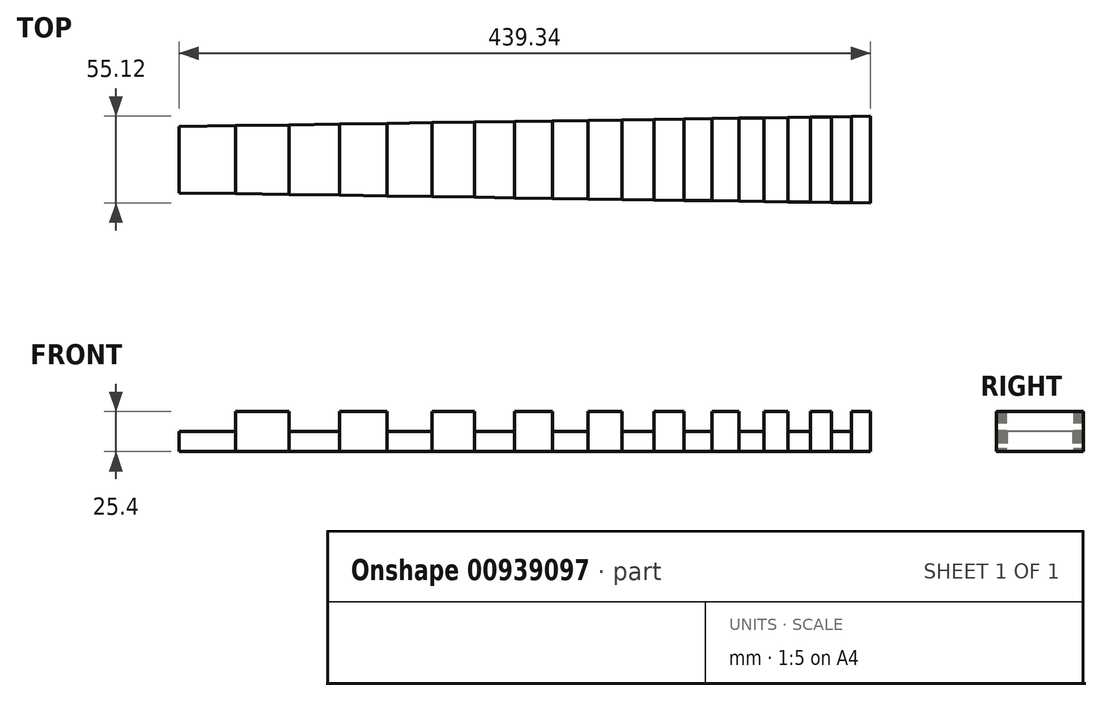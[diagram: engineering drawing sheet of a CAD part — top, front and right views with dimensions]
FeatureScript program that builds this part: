
annotation { "Feature Type Name" : "Feature", "Feature Type Description" : "" }
export const myFeature = defineFeature(function(context is Context, id is Id, definition is map)
    precondition{}
    {
        {
            var Q0;
            Q0=qCreatedBy(makeId("Top.planeOp"),FACE);
            var sketch = newSketch(context, id + "F0", { "sketchPlane" : qUnion([Q0])});
            skLineSegment(sketch, "E0", {"start": v(-189.34, 0) * mm, "end": v(250, 0) * mm});
            skLineSegment(sketch, "E1", {"start": v(-189.34, 21.08) * mm, "end": v(-189.34, -21.08) * mm});
            skPoint(sketch, "E2", {"position": v(-189.34, 0) * mm});
            skLineSegment(sketch, "E3", {"start": v(-153.35, 21.61) * mm, "end": v(-153.35, -21.61) * mm});
            skPoint(sketch, "E4", {"position": v(-153.35, 0) * mm});
            skLineSegment(sketch, "E5", {"start": v(-28.46, 23.45) * mm, "end": v(-28.46, -23.45) * mm});
            skPoint(sketch, "E6", {"position": v(-28.46, 0) * mm});
            skLineSegment(sketch, "E7", {"start": v(-87.31, 22.59) * mm, "end": v(-87.31, -22.59) * mm});
            skPoint(sketch, "E8", {"position": v(-87.31, 0) * mm});
            skLineSegment(sketch, "E9", {"start": v(-57.03, 23.03) * mm, "end": v(-57.03, -23.03) * mm});
            skPoint(sketch, "E10", {"position": v(-57.03, 0) * mm});
            skLineSegment(sketch, "E11", {"start": v(-119.36, 22.11) * mm, "end": v(-119.36, -22.11) * mm});
            skPoint(sketch, "E12", {"position": v(-119.36, 0) * mm});
            skLineSegment(sketch, "E13", {"start": v(112.26, 25.53) * mm, "end": v(112.26, -25.53) * mm});
            skPoint(sketch, "E14", {"position": v(112.26, 0) * mm});
            skLineSegment(sketch, "E15", {"start": v(131.33, 25.8) * mm, "end": v(131.33, -25.8) * mm});
            skPoint(sketch, "E16", {"position": v(131.33, 0) * mm});
            skLineSegment(sketch, "E17", {"start": v(149.34, 26.08) * mm, "end": v(149.34, -26.08) * mm});
            skPoint(sketch, "E18", {"position": v(149.34, 0) * mm});
            skLineSegment(sketch, "E19", {"start": v(166.33, 26.33) * mm, "end": v(166.33, -26.33) * mm});
            skPoint(sketch, "E20", {"position": v(166.33, 0) * mm});
            skLineSegment(sketch, "E21", {"start": v(197.5, 26.78) * mm, "end": v(197.5, -26.78) * mm});
            skPoint(sketch, "E22", {"position": v(197.5, 0) * mm});
            skLineSegment(sketch, "E23", {"start": v(70.65, 24.91) * mm, "end": v(70.65, -24.91) * mm});
            skPoint(sketch, "E24", {"position": v(70.65, 0) * mm});
            skLineSegment(sketch, "E25", {"start": v(92.06, 25.23) * mm, "end": v(92.06, -25.23) * mm});
            skPoint(sketch, "E26", {"position": v(92.06, 0) * mm});
            skLineSegment(sketch, "E27", {"start": v(211.77, 27) * mm, "end": v(211.77, -27) * mm});
            skPoint(sketch, "E28", {"position": v(211.77, 0) * mm});
            skLineSegment(sketch, "E29", {"start": v(250, 27.56) * mm, "end": v(250, -27.56) * mm});
            skPoint(sketch, "E30", {"position": v(250, 0) * mm});
            skLineSegment(sketch, "E31", {"start": v(-189.34, 21.08) * mm, "end": v(250, 27.56) * mm});
            skLineSegment(sketch, "E32", {"start": v(-189.34, -21.08) * mm, "end": v(250, -27.56) * mm});
            skLineSegment(sketch, "E33", {"start": v(-1.48, 23.85) * mm, "end": v(-1.48, -23.85) * mm});
            skPoint(sketch, "E34", {"position": v(-1.48, 0) * mm});
            skLineSegment(sketch, "E35", {"start": v(23.97, 24.23) * mm, "end": v(23.97, -24.23) * mm});
            skPoint(sketch, "E36", {"position": v(23.97, 0) * mm});
            skLineSegment(sketch, "E37", {"start": v(47.97, 24.58) * mm, "end": v(47.97, -24.58) * mm});
            skPoint(sketch, "E38", {"position": v(47.97, 0) * mm});
            skLineSegment(sketch, "E39", {"start": v(182.36, 26.56) * mm, "end": v(182.36, -26.56) * mm});
            skPoint(sketch, "E40", {"position": v(182.36, 0) * mm});
            skLineSegment(sketch, "E41", {"start": v(225.26, 27.2) * mm, "end": v(225.26, -27.2) * mm});
            skPoint(sketch, "E42", {"position": v(225.26, 0) * mm});
            skLineSegment(sketch, "E43", {"start": v(237.99, 27.38) * mm, "end": v(237.99, -27.38) * mm});
            skPoint(sketch, "E44", {"position": v(237.99, 0) * mm});
            skSolve(sketch);
        }
        {
            var Q0;
            {var subQ0=sQuery(id+"F0.wireOp",EDGE,"E3");var subQ1=sQuery(id+"F0.wireOp",EDGE,"E0");var subQ2=makeQuery(id+"F0.imprint","INTERSECT",VERTEX,{"derivedFrom":[subQ1,subQ0]});Q0=makeQuery(id+"F0.imprint","IMPRINT",FACE,{"disambiguationData":[TD([[makeQuery(id+"F0.imprint","IMPRINT",EDGE,{"disambiguationData":[TD([[subQ2,-1.0]])],"derivedFrom":subQ1}),1.0]])]});}
            var Q1;
            {var subQ0=sQuery(id+"F0.wireOp",EDGE,"E3");var subQ1=sQuery(id+"F0.wireOp",EDGE,"E0");var subQ2=makeQuery(id+"F0.imprint","INTERSECT",VERTEX,{"derivedFrom":[subQ1,subQ0]});Q1=makeQuery(id+"F0.imprint","IMPRINT",FACE,{"disambiguationData":[TD([[makeQuery(id+"F0.imprint","IMPRINT",EDGE,{"disambiguationData":[TD([[subQ2,-1.0]])],"derivedFrom":subQ1}),-1.0]])]});}
            var Q2;
            {var subQ0=sQuery(id+"F0.wireOp",EDGE,"E7");var subQ1=sQuery(id+"F0.wireOp",EDGE,"E0");var subQ2=makeQuery(id+"F0.imprint","INTERSECT",VERTEX,{"derivedFrom":[subQ1,subQ0]});Q2=makeQuery(id+"F0.imprint","IMPRINT",FACE,{"disambiguationData":[TD([[makeQuery(id+"F0.imprint","IMPRINT",EDGE,{"disambiguationData":[TD([[subQ2,-1.0]])],"derivedFrom":subQ1}),1.0]])]});}
            var Q3;
            {var subQ0=sQuery(id+"F0.wireOp",EDGE,"E7");var subQ1=sQuery(id+"F0.wireOp",EDGE,"E0");var subQ2=makeQuery(id+"F0.imprint","INTERSECT",VERTEX,{"derivedFrom":[subQ1,subQ0]});Q3=makeQuery(id+"F0.imprint","IMPRINT",FACE,{"disambiguationData":[TD([[makeQuery(id+"F0.imprint","IMPRINT",EDGE,{"disambiguationData":[TD([[subQ2,-1.0]])],"derivedFrom":subQ1}),-1.0]])]});}
            var Q4;
            {var subQ0=sQuery(id+"F0.wireOp",EDGE,"E5");var subQ1=sQuery(id+"F0.wireOp",EDGE,"E0");var subQ2=makeQuery(id+"F0.imprint","INTERSECT",VERTEX,{"derivedFrom":[subQ1,subQ0]});Q4=makeQuery(id+"F0.imprint","IMPRINT",FACE,{"disambiguationData":[TD([[makeQuery(id+"F0.imprint","IMPRINT",EDGE,{"disambiguationData":[TD([[subQ2,-1.0]])],"derivedFrom":subQ1}),1.0]])]});}
            var Q5;
            {var subQ0=sQuery(id+"F0.wireOp",EDGE,"E5");var subQ1=sQuery(id+"F0.wireOp",EDGE,"E0");var subQ2=makeQuery(id+"F0.imprint","INTERSECT",VERTEX,{"derivedFrom":[subQ1,subQ0]});Q5=makeQuery(id+"F0.imprint","IMPRINT",FACE,{"disambiguationData":[TD([[makeQuery(id+"F0.imprint","IMPRINT",EDGE,{"disambiguationData":[TD([[subQ2,-1.0]])],"derivedFrom":subQ1}),-1.0]])]});}
            var Q6;
            {var subQ0=sQuery(id+"F0.wireOp",EDGE,"E35");var subQ1=sQuery(id+"F0.wireOp",EDGE,"E0");var subQ2=makeQuery(id+"F0.imprint","INTERSECT",VERTEX,{"derivedFrom":[subQ1,subQ0]});Q6=makeQuery(id+"F0.imprint","IMPRINT",FACE,{"disambiguationData":[TD([[makeQuery(id+"F0.imprint","IMPRINT",EDGE,{"disambiguationData":[TD([[subQ2,-1.0]])],"derivedFrom":subQ1}),1.0]])]});}
            var Q7;
            {var subQ0=sQuery(id+"F0.wireOp",EDGE,"E35");var subQ1=sQuery(id+"F0.wireOp",EDGE,"E0");var subQ2=makeQuery(id+"F0.imprint","INTERSECT",VERTEX,{"derivedFrom":[subQ1,subQ0]});Q7=makeQuery(id+"F0.imprint","IMPRINT",FACE,{"disambiguationData":[TD([[makeQuery(id+"F0.imprint","IMPRINT",EDGE,{"disambiguationData":[TD([[subQ2,-1.0]])],"derivedFrom":subQ1}),-1.0]])]});}
            var Q8;
            {var subQ0=sQuery(id+"F0.wireOp",EDGE,"E23");var subQ1=sQuery(id+"F0.wireOp",EDGE,"E0");var subQ2=makeQuery(id+"F0.imprint","INTERSECT",VERTEX,{"derivedFrom":[subQ1,subQ0]});Q8=makeQuery(id+"F0.imprint","IMPRINT",FACE,{"disambiguationData":[TD([[makeQuery(id+"F0.imprint","IMPRINT",EDGE,{"disambiguationData":[TD([[subQ2,-1.0]])],"derivedFrom":subQ1}),1.0]])]});}
            var Q9;
            {var subQ0=sQuery(id+"F0.wireOp",EDGE,"E23");var subQ1=sQuery(id+"F0.wireOp",EDGE,"E0");var subQ2=makeQuery(id+"F0.imprint","INTERSECT",VERTEX,{"derivedFrom":[subQ1,subQ0]});Q9=makeQuery(id+"F0.imprint","IMPRINT",FACE,{"disambiguationData":[TD([[makeQuery(id+"F0.imprint","IMPRINT",EDGE,{"disambiguationData":[TD([[subQ2,-1.0]])],"derivedFrom":subQ1}),-1.0]])]});}
            var Q10;
            {var subQ0=sQuery(id+"F0.wireOp",EDGE,"E13");var subQ1=sQuery(id+"F0.wireOp",EDGE,"E0");var subQ2=makeQuery(id+"F0.imprint","INTERSECT",VERTEX,{"derivedFrom":[subQ1,subQ0]});Q10=makeQuery(id+"F0.imprint","IMPRINT",FACE,{"disambiguationData":[TD([[makeQuery(id+"F0.imprint","IMPRINT",EDGE,{"disambiguationData":[TD([[subQ2,-1.0]])],"derivedFrom":subQ1}),1.0]])]});}
            var Q11;
            {var subQ0=sQuery(id+"F0.wireOp",EDGE,"E13");var subQ1=sQuery(id+"F0.wireOp",EDGE,"E0");var subQ2=makeQuery(id+"F0.imprint","INTERSECT",VERTEX,{"derivedFrom":[subQ1,subQ0]});Q11=makeQuery(id+"F0.imprint","IMPRINT",FACE,{"disambiguationData":[TD([[makeQuery(id+"F0.imprint","IMPRINT",EDGE,{"disambiguationData":[TD([[subQ2,-1.0]])],"derivedFrom":subQ1}),-1.0]])]});}
            var Q12;
            {var subQ0=sQuery(id+"F0.wireOp",EDGE,"E17");var subQ1=sQuery(id+"F0.wireOp",EDGE,"E0");var subQ2=makeQuery(id+"F0.imprint","INTERSECT",VERTEX,{"derivedFrom":[subQ1,subQ0]});Q12=makeQuery(id+"F0.imprint","IMPRINT",FACE,{"disambiguationData":[TD([[makeQuery(id+"F0.imprint","IMPRINT",EDGE,{"disambiguationData":[TD([[subQ2,-1.0]])],"derivedFrom":subQ1}),1.0]])]});}
            var Q13;
            {var subQ0=sQuery(id+"F0.wireOp",EDGE,"E17");var subQ1=sQuery(id+"F0.wireOp",EDGE,"E0");var subQ2=makeQuery(id+"F0.imprint","INTERSECT",VERTEX,{"derivedFrom":[subQ1,subQ0]});Q13=makeQuery(id+"F0.imprint","IMPRINT",FACE,{"disambiguationData":[TD([[makeQuery(id+"F0.imprint","IMPRINT",EDGE,{"disambiguationData":[TD([[subQ2,-1.0]])],"derivedFrom":subQ1}),-1.0]])]});}
            var Q14;
            {var subQ0=sQuery(id+"F0.wireOp",EDGE,"E39");var subQ1=sQuery(id+"F0.wireOp",EDGE,"E0");var subQ2=makeQuery(id+"F0.imprint","INTERSECT",VERTEX,{"derivedFrom":[subQ1,subQ0]});Q14=makeQuery(id+"F0.imprint","IMPRINT",FACE,{"disambiguationData":[TD([[makeQuery(id+"F0.imprint","IMPRINT",EDGE,{"disambiguationData":[TD([[subQ2,-1.0]])],"derivedFrom":subQ1}),1.0]])]});}
            var Q15;
            {var subQ0=sQuery(id+"F0.wireOp",EDGE,"E39");var subQ1=sQuery(id+"F0.wireOp",EDGE,"E0");var subQ2=makeQuery(id+"F0.imprint","INTERSECT",VERTEX,{"derivedFrom":[subQ1,subQ0]});Q15=makeQuery(id+"F0.imprint","IMPRINT",FACE,{"disambiguationData":[TD([[makeQuery(id+"F0.imprint","IMPRINT",EDGE,{"disambiguationData":[TD([[subQ2,-1.0]])],"derivedFrom":subQ1}),-1.0]])]});}
            var Q16;
            {var subQ0=sQuery(id+"F0.wireOp",EDGE,"E27");var subQ1=sQuery(id+"F0.wireOp",EDGE,"E0");var subQ2=makeQuery(id+"F0.imprint","INTERSECT",VERTEX,{"derivedFrom":[subQ1,subQ0]});Q16=makeQuery(id+"F0.imprint","IMPRINT",FACE,{"disambiguationData":[TD([[makeQuery(id+"F0.imprint","IMPRINT",EDGE,{"disambiguationData":[TD([[subQ2,-1.0]])],"derivedFrom":subQ1}),1.0]])]});}
            var Q17;
            {var subQ0=sQuery(id+"F0.wireOp",EDGE,"E27");var subQ1=sQuery(id+"F0.wireOp",EDGE,"E0");var subQ2=makeQuery(id+"F0.imprint","INTERSECT",VERTEX,{"derivedFrom":[subQ1,subQ0]});Q17=makeQuery(id+"F0.imprint","IMPRINT",FACE,{"disambiguationData":[TD([[makeQuery(id+"F0.imprint","IMPRINT",EDGE,{"disambiguationData":[TD([[subQ2,-1.0]])],"derivedFrom":subQ1}),-1.0]])]});}
            var Q18;
            {var subQ0=sQuery(id+"F0.wireOp",EDGE,"E29");var subQ1=sQuery(id+"F0.wireOp",EDGE,"E0");var subQ2=makeQuery(id+"F0.imprint","INTERSECT",VERTEX,{"derivedFrom":[subQ1,subQ0]});Q18=makeQuery(id+"F0.imprint","IMPRINT",FACE,{"disambiguationData":[TD([[makeQuery(id+"F0.imprint","IMPRINT",EDGE,{"disambiguationData":[TD([[subQ2,1.0]])],"derivedFrom":subQ1}),1.0]])]});}
            var Q19;
            {var subQ0=sQuery(id+"F0.wireOp",EDGE,"E29");var subQ1=sQuery(id+"F0.wireOp",EDGE,"E0");var subQ2=makeQuery(id+"F0.imprint","INTERSECT",VERTEX,{"derivedFrom":[subQ1,subQ0]});Q19=makeQuery(id+"F0.imprint","IMPRINT",FACE,{"disambiguationData":[TD([[makeQuery(id+"F0.imprint","IMPRINT",EDGE,{"disambiguationData":[TD([[subQ2,1.0]])],"derivedFrom":subQ1}),-1.0]])]});}
            extrude(context, id + "F1", {"entities" : qUnion([Q0, Q1, Q2, Q3, Q4, Q5, Q6, Q7, Q8, Q9, Q10, Q11, Q12, Q13, Q14, Q15, Q16, Q17, Q18, Q19]), "depth" : 25.4 * mm, "offsetDistance" : 25.4 * mm});
        }
        {
            var Q0;
            {var subQ0=sQuery(id+"F0.wireOp",EDGE,"E1");var subQ1=sQuery(id+"F0.wireOp",EDGE,"E0");var subQ2=makeQuery(id+"F0.imprint","INTERSECT",VERTEX,{"derivedFrom":[subQ1,subQ0]});Q0=makeQuery(id+"F0.imprint","IMPRINT",FACE,{"disambiguationData":[TD([[makeQuery(id+"F0.imprint","IMPRINT",EDGE,{"disambiguationData":[TD([[subQ2,-1.0]])],"derivedFrom":subQ1}),1.0]])]});}
            var Q1;
            {var subQ0=sQuery(id+"F0.wireOp",EDGE,"E1");var subQ1=sQuery(id+"F0.wireOp",EDGE,"E0");var subQ2=makeQuery(id+"F0.imprint","INTERSECT",VERTEX,{"derivedFrom":[subQ1,subQ0]});Q1=makeQuery(id+"F0.imprint","IMPRINT",FACE,{"disambiguationData":[TD([[makeQuery(id+"F0.imprint","IMPRINT",EDGE,{"disambiguationData":[TD([[subQ2,-1.0]])],"derivedFrom":subQ1}),-1.0]])]});}
            var Q2;
            {var subQ0=sQuery(id+"F0.wireOp",EDGE,"E11");var subQ1=sQuery(id+"F0.wireOp",EDGE,"E0");var subQ2=makeQuery(id+"F0.imprint","INTERSECT",VERTEX,{"derivedFrom":[subQ1,subQ0]});Q2=makeQuery(id+"F0.imprint","IMPRINT",FACE,{"disambiguationData":[TD([[makeQuery(id+"F0.imprint","IMPRINT",EDGE,{"disambiguationData":[TD([[subQ2,-1.0]])],"derivedFrom":subQ1}),1.0]])]});}
            var Q3;
            {var subQ0=sQuery(id+"F0.wireOp",EDGE,"E11");var subQ1=sQuery(id+"F0.wireOp",EDGE,"E0");var subQ2=makeQuery(id+"F0.imprint","INTERSECT",VERTEX,{"derivedFrom":[subQ1,subQ0]});Q3=makeQuery(id+"F0.imprint","IMPRINT",FACE,{"disambiguationData":[TD([[makeQuery(id+"F0.imprint","IMPRINT",EDGE,{"disambiguationData":[TD([[subQ2,-1.0]])],"derivedFrom":subQ1}),-1.0]])]});}
            var Q4;
            {var subQ0=sQuery(id+"F0.wireOp",EDGE,"E9");var subQ1=sQuery(id+"F0.wireOp",EDGE,"E0");var subQ2=makeQuery(id+"F0.imprint","INTERSECT",VERTEX,{"derivedFrom":[subQ1,subQ0]});Q4=makeQuery(id+"F0.imprint","IMPRINT",FACE,{"disambiguationData":[TD([[makeQuery(id+"F0.imprint","IMPRINT",EDGE,{"disambiguationData":[TD([[subQ2,-1.0]])],"derivedFrom":subQ1}),1.0]])]});}
            var Q5;
            {var subQ0=sQuery(id+"F0.wireOp",EDGE,"E9");var subQ1=sQuery(id+"F0.wireOp",EDGE,"E0");var subQ2=makeQuery(id+"F0.imprint","INTERSECT",VERTEX,{"derivedFrom":[subQ1,subQ0]});Q5=makeQuery(id+"F0.imprint","IMPRINT",FACE,{"disambiguationData":[TD([[makeQuery(id+"F0.imprint","IMPRINT",EDGE,{"disambiguationData":[TD([[subQ2,-1.0]])],"derivedFrom":subQ1}),-1.0]])]});}
            var Q6;
            {var subQ0=sQuery(id+"F0.wireOp",EDGE,"E33");var subQ1=sQuery(id+"F0.wireOp",EDGE,"E0");var subQ2=makeQuery(id+"F0.imprint","INTERSECT",VERTEX,{"derivedFrom":[subQ1,subQ0]});Q6=makeQuery(id+"F0.imprint","IMPRINT",FACE,{"disambiguationData":[TD([[makeQuery(id+"F0.imprint","IMPRINT",EDGE,{"disambiguationData":[TD([[subQ2,-1.0]])],"derivedFrom":subQ1}),1.0]])]});}
            var Q7;
            {var subQ0=sQuery(id+"F0.wireOp",EDGE,"E33");var subQ1=sQuery(id+"F0.wireOp",EDGE,"E0");var subQ2=makeQuery(id+"F0.imprint","INTERSECT",VERTEX,{"derivedFrom":[subQ1,subQ0]});Q7=makeQuery(id+"F0.imprint","IMPRINT",FACE,{"disambiguationData":[TD([[makeQuery(id+"F0.imprint","IMPRINT",EDGE,{"disambiguationData":[TD([[subQ2,-1.0]])],"derivedFrom":subQ1}),-1.0]])]});}
            var Q8;
            {var subQ0=sQuery(id+"F0.wireOp",EDGE,"E37");var subQ1=sQuery(id+"F0.wireOp",EDGE,"E0");var subQ2=makeQuery(id+"F0.imprint","INTERSECT",VERTEX,{"derivedFrom":[subQ1,subQ0]});Q8=makeQuery(id+"F0.imprint","IMPRINT",FACE,{"disambiguationData":[TD([[makeQuery(id+"F0.imprint","IMPRINT",EDGE,{"disambiguationData":[TD([[subQ2,-1.0]])],"derivedFrom":subQ1}),1.0]])]});}
            var Q9;
            {var subQ0=sQuery(id+"F0.wireOp",EDGE,"E37");var subQ1=sQuery(id+"F0.wireOp",EDGE,"E0");var subQ2=makeQuery(id+"F0.imprint","INTERSECT",VERTEX,{"derivedFrom":[subQ1,subQ0]});Q9=makeQuery(id+"F0.imprint","IMPRINT",FACE,{"disambiguationData":[TD([[makeQuery(id+"F0.imprint","IMPRINT",EDGE,{"disambiguationData":[TD([[subQ2,-1.0]])],"derivedFrom":subQ1}),-1.0]])]});}
            var Q10;
            {var subQ0=sQuery(id+"F0.wireOp",EDGE,"E25");var subQ1=sQuery(id+"F0.wireOp",EDGE,"E0");var subQ2=makeQuery(id+"F0.imprint","INTERSECT",VERTEX,{"derivedFrom":[subQ1,subQ0]});Q10=makeQuery(id+"F0.imprint","IMPRINT",FACE,{"disambiguationData":[TD([[makeQuery(id+"F0.imprint","IMPRINT",EDGE,{"disambiguationData":[TD([[subQ2,-1.0]])],"derivedFrom":subQ1}),1.0]])]});}
            var Q11;
            {var subQ0=sQuery(id+"F0.wireOp",EDGE,"E25");var subQ1=sQuery(id+"F0.wireOp",EDGE,"E0");var subQ2=makeQuery(id+"F0.imprint","INTERSECT",VERTEX,{"derivedFrom":[subQ1,subQ0]});Q11=makeQuery(id+"F0.imprint","IMPRINT",FACE,{"disambiguationData":[TD([[makeQuery(id+"F0.imprint","IMPRINT",EDGE,{"disambiguationData":[TD([[subQ2,-1.0]])],"derivedFrom":subQ1}),-1.0]])]});}
            var Q12;
            {var subQ0=sQuery(id+"F0.wireOp",EDGE,"E15");var subQ1=sQuery(id+"F0.wireOp",EDGE,"E0");var subQ2=makeQuery(id+"F0.imprint","INTERSECT",VERTEX,{"derivedFrom":[subQ1,subQ0]});Q12=makeQuery(id+"F0.imprint","IMPRINT",FACE,{"disambiguationData":[TD([[makeQuery(id+"F0.imprint","IMPRINT",EDGE,{"disambiguationData":[TD([[subQ2,-1.0]])],"derivedFrom":subQ1}),1.0]])]});}
            var Q13;
            {var subQ0=sQuery(id+"F0.wireOp",EDGE,"E15");var subQ1=sQuery(id+"F0.wireOp",EDGE,"E0");var subQ2=makeQuery(id+"F0.imprint","INTERSECT",VERTEX,{"derivedFrom":[subQ1,subQ0]});Q13=makeQuery(id+"F0.imprint","IMPRINT",FACE,{"disambiguationData":[TD([[makeQuery(id+"F0.imprint","IMPRINT",EDGE,{"disambiguationData":[TD([[subQ2,-1.0]])],"derivedFrom":subQ1}),-1.0]])]});}
            var Q14;
            {var subQ0=sQuery(id+"F0.wireOp",EDGE,"E19");var subQ1=sQuery(id+"F0.wireOp",EDGE,"E0");var subQ2=makeQuery(id+"F0.imprint","INTERSECT",VERTEX,{"derivedFrom":[subQ1,subQ0]});Q14=makeQuery(id+"F0.imprint","IMPRINT",FACE,{"disambiguationData":[TD([[makeQuery(id+"F0.imprint","IMPRINT",EDGE,{"disambiguationData":[TD([[subQ2,-1.0]])],"derivedFrom":subQ1}),1.0]])]});}
            var Q15;
            {var subQ0=sQuery(id+"F0.wireOp",EDGE,"E19");var subQ1=sQuery(id+"F0.wireOp",EDGE,"E0");var subQ2=makeQuery(id+"F0.imprint","INTERSECT",VERTEX,{"derivedFrom":[subQ1,subQ0]});Q15=makeQuery(id+"F0.imprint","IMPRINT",FACE,{"disambiguationData":[TD([[makeQuery(id+"F0.imprint","IMPRINT",EDGE,{"disambiguationData":[TD([[subQ2,-1.0]])],"derivedFrom":subQ1}),-1.0]])]});}
            var Q16;
            {var subQ0=sQuery(id+"F0.wireOp",EDGE,"E21");var subQ1=sQuery(id+"F0.wireOp",EDGE,"E0");var subQ2=makeQuery(id+"F0.imprint","INTERSECT",VERTEX,{"derivedFrom":[subQ1,subQ0]});Q16=makeQuery(id+"F0.imprint","IMPRINT",FACE,{"disambiguationData":[TD([[makeQuery(id+"F0.imprint","IMPRINT",EDGE,{"disambiguationData":[TD([[subQ2,-1.0]])],"derivedFrom":subQ1}),1.0]])]});}
            var Q17;
            {var subQ0=sQuery(id+"F0.wireOp",EDGE,"E21");var subQ1=sQuery(id+"F0.wireOp",EDGE,"E0");var subQ2=makeQuery(id+"F0.imprint","INTERSECT",VERTEX,{"derivedFrom":[subQ1,subQ0]});Q17=makeQuery(id+"F0.imprint","IMPRINT",FACE,{"disambiguationData":[TD([[makeQuery(id+"F0.imprint","IMPRINT",EDGE,{"disambiguationData":[TD([[subQ2,-1.0]])],"derivedFrom":subQ1}),-1.0]])]});}
            var Q18;
            {var subQ0=sQuery(id+"F0.wireOp",EDGE,"E41");var subQ1=sQuery(id+"F0.wireOp",EDGE,"E0");var subQ2=makeQuery(id+"F0.imprint","INTERSECT",VERTEX,{"derivedFrom":[subQ1,subQ0]});Q18=makeQuery(id+"F0.imprint","IMPRINT",FACE,{"disambiguationData":[TD([[makeQuery(id+"F0.imprint","IMPRINT",EDGE,{"disambiguationData":[TD([[subQ2,-1.0]])],"derivedFrom":subQ1}),1.0]])]});}
            var Q19;
            {var subQ0=sQuery(id+"F0.wireOp",EDGE,"E41");var subQ1=sQuery(id+"F0.wireOp",EDGE,"E0");var subQ2=makeQuery(id+"F0.imprint","INTERSECT",VERTEX,{"derivedFrom":[subQ1,subQ0]});Q19=makeQuery(id+"F0.imprint","IMPRINT",FACE,{"disambiguationData":[TD([[makeQuery(id+"F0.imprint","IMPRINT",EDGE,{"disambiguationData":[TD([[subQ2,-1.0]])],"derivedFrom":subQ1}),-1.0]])]});}
            extrude(context, id + "F2", {"entities" : qUnion([Q0, Q1, Q2, Q3, Q4, Q5, Q6, Q7, Q8, Q9, Q10, Q11, Q12, Q13, Q14, Q15, Q16, Q17, Q18, Q19]), "depth" : 12.7 * mm, "offsetDistance" : 25.4 * mm});
        }
    });
